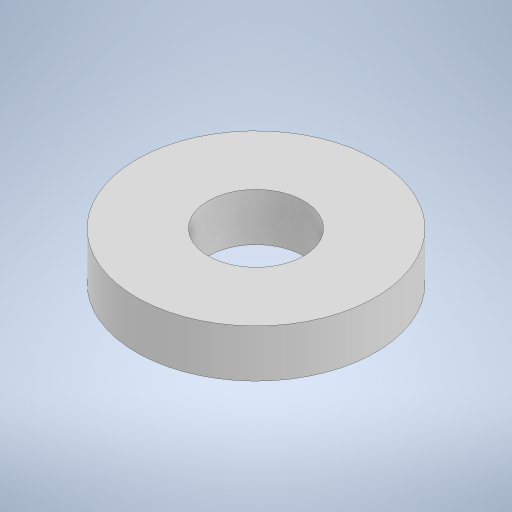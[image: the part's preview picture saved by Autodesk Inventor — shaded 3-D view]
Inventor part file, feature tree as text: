
AUTODESK INVENTOR PART (.ipt)
format: ipt  version: 2023 (Build 270158000, 158)  size: 209,920 bytes
history: native  units: mm
features: other x1, extrude x1, sketch x1
ambient origin geometry x8: Origin, YZ Plane, XZ Plane, XY Plane, X Axis, Y Axis, Z Axis, Center Point
bodies: Body1 (feature_tree)
feature tree (3):
  other  "Твердое тело1"
  extrude  "Выдавливание1"  Depth=4.0mm
  sketch  "Эскиз1"
